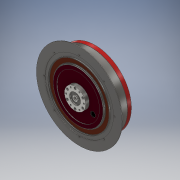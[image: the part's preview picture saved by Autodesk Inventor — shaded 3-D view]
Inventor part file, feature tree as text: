
AUTODESK INVENTOR PART (.ipt)
format: ipt  version: 2018 (Build 220112000, 112)  size: 435,712 bytes
history: native  units: mm
features: sketch x17, thread x13, extrude x12, hole x4, pattern_circular x4, projected_geometry x3, revolve x2, plane x1, chamfer x1
ambient origin geometry x8: Origin, YZ Plane, XZ Plane, XY Plane, X Axis, Y Axis, Z Axis, Center Point
bodies: Solid1 (feature_tree)
feature tree (57):
  extrude  "Extrusion1"  Depth=14.0mm TaperAngle=0.0deg
  extrude  "Extrusion2"  Depth=42.0mm TaperAngle=0.0deg
  extrude  "Extrusion3"  Depth=21.5mm TaperAngle=0.0deg
  extrude  "Extrusion4"  Depth=13.5mm TaperAngle=0.0deg
  thread  "Thread1"  [1 undecoded]
  sketch  "Sketch5"  dims[d16=116.0mm d18=8.0mm]
  extrude  "Extrusion5"  Depth=8.0mm
  extrude  "Extrusion6"  Depth=8.0mm
  hole  "Hole1"  [1 undecoded]
  pattern_circular  "Circular Pattern1"  Count=6 Angle=360.0deg
  extrude  "Extrusion7"  Depth=6.0mm
  extrude  "Extrusion8"  Depth=80.0mm TaperAngle=360.0deg
  plane  "Work Plane1"
  revolve  "Revolution1"  Angle=360.0deg
  extrude  "Extrusion9"  Depth=17.0mm TaperAngle=0.0deg
  chamfer  "Chamfer1"  Distance=4.0mm
  revolve  "Revolution2"  [1 undecoded]
  hole  "Hole2"  [1 undecoded]
  pattern_circular  "Circular Pattern2"  [2 undecoded]
  hole  "Hole3"  [1 undecoded]
  thread  "Thread2"  [1 undecoded]
  pattern_circular  "Circular Pattern3"  [2 undecoded]
  hole  "Hole4"  [1 undecoded]
  pattern_circular  "Circular Pattern4"  Angle=45.0deg  [1 undecoded]
  thread  "Thread3"  [1 undecoded]
  thread  "Thread4"  [1 undecoded]
  thread  "Thread5"  [1 undecoded]
  thread  "Thread6"  [1 undecoded]
  thread  "Thread7"  [1 undecoded]
  thread  "Thread8"  [1 undecoded]
  thread  "Thread9"  [1 undecoded]
  thread  "Thread10"  [1 undecoded]
  thread  "Thread11"  [1 undecoded]
  thread  "Thread12"  [1 undecoded]
  thread  "Thread13"  [1 undecoded]
  extrude  "Extrusion10"  Depth=60.0mm TaperAngle=360.0deg
  extrude  "Extrusion11"  Depth=10.0mm TaperAngle=0.0deg
  extrude  "Extrusion12"  Depth=10.0mm TaperAngle=0.0deg
  sketch  "Sketch1"  dims[d0=262.0mm d1=14.0mm d2=0.0mm]
  sketch  "Sketch2"  dims[d3=261.0mm d4=42.0mm d5=0.0mm]
  sketch  "Sketch3"  dims[d6=94.0mm d7=21.5mm d8=0.0mm]
  sketch  "Sketch4"  dims[d9=73.0mm d10=13.5mm d11=0.0mm d12=10.0mm d13=0.0mm]
  sketch  "Sketch6"  dims[d20=8.0mm d21=8.0mm]
  sketch  "Sketch7"  dims[d22=30.0mm d24=360.0deg d26=4.0mm d27=0.0mm]
  sketch  "Sketch8"  dims[d28=8.0mm d29=60.0mm d31=360.0deg]
  sketch  "Sketch9"  dims[d33=10.0mm d34=0.0mm d35=6.0mm]
  sketch  "Sketch10"  dims[d36=127.5mm d37=80.0mm d39=360.0deg]
  sketch  "Sketch11"  dims[d41=3.0mm d42=6.0mm d43=6.0mm d44=2.0mm d45=90.0deg d46=8.0mm d47=20.594885mm d48=80.0mm d49=360.0deg]
  sketch  "Sketch12"  dims[d51=77.0mm d52=17.0mm d53=0.0mm]
  sketch  "Sketch13"  dims[d54=180.0mm d55=4.0mm d56=0.0mm]
  sketch  "Sketch14"  dims[d57=0.0mm d58=1.0mm]
  sketch  "Sketch15"  dims[d59=1.0mm d60=1.5mm]
  sketch  "Sketch16"  dims[d61=4.0mm]
  sketch  "Sketch17"  dims[d62=15.0mm d63=1.0mm d64=1.5mm d65=90.0deg d66=65.0mm d67=20.0mm d68=0.0mm d69=2.0mm d70=2.0mm d71=45.0deg d72=2.0mm d73=155.0mm d74=124.0mm d75=90.0deg d76=3.0mm d77=6.0mm d78=6.0mm d79=2.0mm d80=90.0deg d81=8.0mm d82=20.594885mm d83=80.0mm d84=360.0deg d86=64.0mm d87=8.0mm d88=8.0mm d89=6.0mm d90=4.0mm d91=2.0mm d92=90.0deg d93=8.0mm d94=0.0mm d95=10.0mm d96=0.0mm d97=60.0mm d98=360.0deg d100=64.0mm d101=5.0mm d102=5.0mm d103=6.0mm d104=4.0mm d105=2.0mm d106=90.0deg d107=8.0mm d108=0.0mm d109=60.0mm d110=360.0deg d112=10.0mm d113=0.0mm d114=10.0mm d115=0.0mm d116=10.0mm d117=0.0mm d118=10.0mm d119=0.0mm d120=10.0mm d121=0.0mm d122=10.0mm d123=0.0mm d124=10.0mm d125=0.0mm d126=10.0mm d127=0.0mm d128=10.0mm d129=0.0mm d130=10.0mm d131=0.0mm d132=10.0mm d133=0.0mm d134=40.0mm d135=20.0mm d136=10.0mm d137=5.0mm d138=0.0mm d139=155.0mm d140=2.0mm d141=0.0mm d142=18.0mm d143=2.0mm d144=0.0mm]
  projected_geometry  "Projected Loop1"
  projected_geometry  "Projected Loop2"
  projected_geometry  "Projected Loop3"
note: 23 required parameter values undecoded (feature->parameter linkage not recoverable at this tier; creation-order binding heuristic only, values carry confidence <= 0.55)